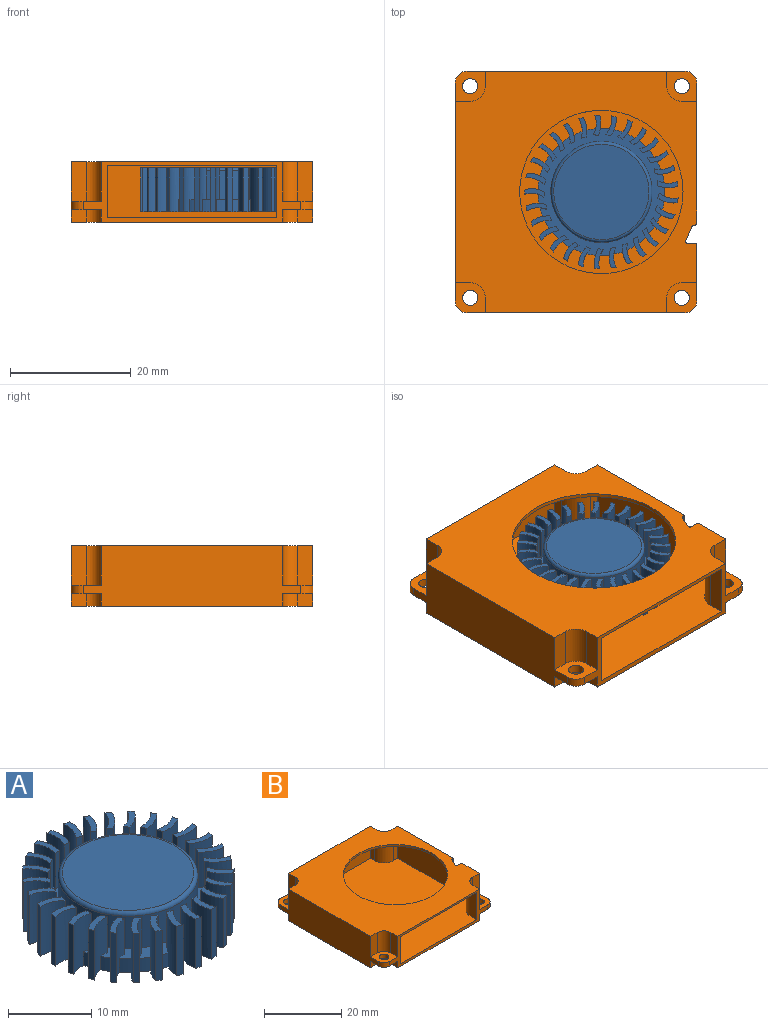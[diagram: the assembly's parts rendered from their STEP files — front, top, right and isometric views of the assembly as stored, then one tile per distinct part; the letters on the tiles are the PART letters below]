
ASSEMBLY  parts=2 mates=1
PART A: 179 faces, bbox 25.4x25.4x7.3 mm
  f0: plane 21x20.99mm, normal (0,0,1), area 101.2mm2, adj f1,f2,f3,f4,f5,f6,f7,f8
  f1: cylinder r=10.5mm len=2mm, axis (0,0,-1), area 3mm2, adj f0,f30,f172,f175
  f2: cylinder r=10.5mm len=2mm, axis (0,0,-1), area 3mm2, adj f0,f30,f167,f170
  f3: cylinder r=10.5mm len=2mm, axis (0,0,-1), area 3mm2, adj f0,f30,f162,f165
  f4: cylinder r=10.5mm len=2mm, axis (0,0,-1), area 3mm2, adj f0,f30,f157,f160
  f5: cylinder r=10.5mm len=2mm, axis (0,0,-1), area 3mm2, adj f0,f30,f152,f155
  f6: cylinder r=10.5mm len=2mm, axis (0,0,-1), area 3mm2, adj f0,f30,f147,f150
  f7: cylinder r=10.5mm len=2mm, axis (0,0,-1), area 3mm2, adj f0,f30,f142,f145
  f8: cylinder r=10.5mm len=2mm, axis (0,0,-1), area 3mm2, adj f0,f30,f137,f140
  f9: cylinder r=10.5mm len=2mm, axis (0,0,-1), area 3mm2, adj f0,f30,f132,f135
  f10: cylinder r=10.5mm len=2mm, axis (0,0,-1), area 3mm2, adj f0,f30,f127,f130
  f11: cylinder r=10.5mm len=2mm, axis (0,0,-1), area 3mm2, adj f0,f30,f122,f125
  f12: cylinder r=10.5mm len=2mm, axis (0,0,-1), area 3mm2, adj f0,f30,f117,f120
  f13: cylinder r=10.5mm len=2mm, axis (0,0,-1), area 3mm2, adj f0,f30,f112,f115
  f14: cylinder r=10.5mm len=2mm, axis (0,0,-1), area 3mm2, adj f0,f30,f107,f110
  f15: cylinder r=10.5mm len=2mm, axis (0,0,-1), area 3mm2, adj f0,f30,f102,f105
  f16: cylinder r=10.5mm len=2mm, axis (0,0,-1), area 3mm2, adj f0,f30,f97,f100
  f17: cylinder r=10.5mm len=2mm, axis (0,0,-1), area 3mm2, adj f0,f30,f92,f95
  f18: cylinder r=10.5mm len=2mm, axis (0,0,-1), area 3mm2, adj f0,f30,f87,f90
  f19: cylinder r=10.5mm len=2mm, axis (0,0,-1), area 3mm2, adj f0,f30,f82,f85
  f20: cylinder r=10.5mm len=2mm, axis (0,0,-1), area 3mm2, adj f0,f30,f77,f80
  f21: cylinder r=10.5mm len=2mm, axis (0,0,-1), area 3mm2, adj f0,f30,f72,f75
  f22: cylinder r=10.5mm len=2mm, axis (0,0,-1), area 3mm2, adj f0,f30,f67,f70
  f23: cylinder r=10.5mm len=2mm, axis (0,0,-1), area 3mm2, adj f0,f30,f62,f65
  f24: cylinder r=10.5mm len=2mm, axis (0,0,-1), area 3mm2, adj f0,f30,f57,f60
  f25: cylinder r=10.5mm len=2mm, axis (0,0,-1), area 3mm2, adj f0,f30,f52,f55
  f26: cylinder r=10.5mm len=2mm, axis (0,0,-1), area 3mm2, adj f0,f30,f47,f50
  f27: cylinder r=10.5mm len=2mm, axis (0,0,-1), area 3mm2, adj f0,f30,f42,f45
  f28: cylinder r=10.5mm len=2mm, axis (0,0,-1), area 3mm2, adj f0,f30,f34,f40
  f29: cylinder r=10.5mm len=2mm, axis (0,0,-1), area 3mm2, adj f0,f30,f33,f177
  f30: plane 25.4x25.4mm, normal (0,0,-1), area 394.2mm2, adj f1,f2,f3,f4,f5,f6,f7,f8
  f31: cylinder r=8.38mm len=16.75mm, axis (0,0,-1), area 250mm2, adj f0,f178
  f32: plane 15.75x15.75mm, normal (0,0,1), area 194.8mm2, adj f178
  f33: cylinder r=4.5mm len=7.25mm, axis (0,0,-1), area 21.8mm2, adj f0,f29,f30,f35,f36,f37
  f34: cylinder r=3.75mm len=7.25mm, axis (0,0,-1), area 22.2mm2, adj f0,f28,f30,f35,f36,f37
  f35: plane 3.36x1.87mm, normal (0,0,1), area 2.5mm2, adj f33,f34,f36,f37
  f36: plane 7.25x0.75mm, normal (-0.37,0.93,0), area 5.8mm2, adj f30,f33,f34,f35
  f37: plane 5.25x0.77mm, normal (0.37,-0.93,0), area 4.4mm2, adj f0,f33,f34,f35
  f38: plane 3.21x2.41mm, normal (0,0,1), area 2.5mm2, adj f39,f40,f41,f42
  f39: plane 7.25x0.67mm, normal (-0.56,0.83,0), area 5.8mm2, adj f30,f38,f40,f42
  f40: cylinder r=4.5mm len=7.25mm, axis (0,0,-1), area 21.8mm2, adj f0,f28,f30,f38,f39,f41
  f41: plane 5.25x0.69mm, normal (0.56,-0.83,0), area 4.4mm2, adj f0,f38,f40,f42
  f42: cylinder r=3.75mm len=7.25mm, axis (0,0,-1), area 22.2mm2, adj f0,f27,f30,f38,f39,f41
  f43: plane 2.91x2.85mm, normal (0,0,1), area 2.5mm2, adj f44,f45,f46,f47
  f44: plane 7.25x0.59mm, normal (-0.73,0.69,0), area 5.8mm2, adj f30,f43,f45,f47
  f45: cylinder r=4.5mm len=7.25mm, axis (0,0,-1), area 21.8mm2, adj f0,f27,f30,f43,f44,f46
  f46: plane 5.25x0.6mm, normal (0.73,-0.69,0), area 4.4mm2, adj f0,f43,f45,f47
  f47: cylinder r=3.75mm len=7.25mm, axis (0,0,-1), area 22.2mm2, adj f0,f26,f30,f43,f44,f46
  f48: plane 3.15x2.47mm, normal (0,0,1), area 2.5mm2, adj f49,f50,f51,f52
  f49: plane 7.25x0.69mm, normal (-0.86,0.51,0), area 5.8mm2, adj f30,f48,f50,f52
  f50: cylinder r=4.5mm len=7.25mm, axis (0,0,-1), area 21.8mm2, adj f0,f26,f30,f48,f49,f51
  f51: plane 5.25x0.71mm, normal (0.86,-0.51,0), area 4.4mm2, adj f0,f48,f50,f52
  f52: cylinder r=3.75mm len=7.25mm, axis (0,0,-1), area 22.2mm2, adj f0,f25,f30,f48,f49,f51
  f53: plane 3.31x1.91mm, normal (0,0,1), area 2.5mm2, adj f54,f55,f56,f57
  f54: plane 7.25x0.76mm, normal (-0.95,0.32,0), area 5.8mm2, adj f30,f53,f55,f57
  f55: cylinder r=4.5mm len=7.25mm, axis (0,0,-1), area 21.8mm2, adj f0,f25,f30,f53,f54,f56
  f56: plane 5.25x0.79mm, normal (0.95,-0.32,0), area 4.4mm2, adj f0,f53,f55,f57
  f57: cylinder r=3.75mm len=7.25mm, axis (0,0,-1), area 22.2mm2, adj f0,f24,f30,f53,f54,f56
  f58: plane 3.31x1.39mm, normal (0,0,1), area 2.5mm2, adj f59,f60,f61,f62
  f59: plane 7.25x0.8mm, normal (-0.99,0.11,0), area 5.8mm2, adj f30,f58,f60,f62
  f60: cylinder r=4.5mm len=7.25mm, axis (0,0,-1), area 21.8mm2, adj f0,f24,f30,f58,f59,f61
  f61: plane 5.25x0.82mm, normal (0.99,-0.11,0), area 4.4mm2, adj f0,f58,f60,f62
  f62: cylinder r=3.75mm len=7.25mm, axis (0,0,-1), area 22.2mm2, adj f0,f23,f30,f58,f59,f61
  f63: plane 3.33x1.25mm, normal (0,0,1), area 2.5mm2, adj f64,f65,f66,f67
  f64: plane 7.25x0.8mm, normal (-0.99,-0.11,0), area 5.8mm2, adj f30,f63,f65,f67
  f65: cylinder r=4.5mm len=7.25mm, axis (0,0,-1), area 21.8mm2, adj f0,f23,f30,f63,f64,f66
  f66: plane 5.25x0.82mm, normal (0.99,0.11,0), area 4.4mm2, adj f0,f63,f65,f67
  f67: cylinder r=3.75mm len=7.25mm, axis (0,0,-1), area 22.2mm2, adj f0,f22,f30,f63,f64,f66
  f68: plane 3.38x1.73mm, normal (0,0,1), area 2.5mm2, adj f69,f70,f71,f72
  f69: plane 7.25x0.76mm, normal (-0.95,-0.32,0), area 5.8mm2, adj f30,f68,f70,f72
  f70: cylinder r=4.5mm len=7.25mm, axis (0,0,-1), area 21.8mm2, adj f0,f22,f30,f68,f69,f71
  f71: plane 5.25x0.79mm, normal (0.95,0.32,0), area 4.4mm2, adj f0,f68,f70,f72
  f72: cylinder r=3.75mm len=7.25mm, axis (0,0,-1), area 22.2mm2, adj f0,f21,f30,f68,f69,f71
  f73: plane 3.26x2.29mm, normal (0,0,1), area 2.5mm2, adj f74,f75,f76,f77
  f74: plane 7.25x0.69mm, normal (-0.86,-0.52,0), area 5.8mm2, adj f30,f73,f75,f77
  f75: cylinder r=4.5mm len=7.25mm, axis (0,0,-1), area 21.8mm2, adj f0,f21,f30,f73,f74,f76
  f76: plane 5.25x0.71mm, normal (0.86,0.52,0), area 4.4mm2, adj f0,f73,f75,f77
  f77: cylinder r=3.75mm len=7.25mm, axis (0,0,-1), area 22.2mm2, adj f0,f20,f30,f73,f74,f76
  f78: plane 2.99x2.75mm, normal (0,0,1), area 2.5mm2, adj f79,f80,f81,f82
  f79: plane 7.25x0.58mm, normal (-0.73,-0.69,0), area 5.8mm2, adj f30,f78,f80,f82
  f80: cylinder r=4.5mm len=7.25mm, axis (0,0,-1), area 21.8mm2, adj f0,f20,f30,f78,f79,f81
  f81: plane 5.25x0.6mm, normal (0.73,0.69,0), area 4.4mm2, adj f0,f78,f80,f82
  f82: cylinder r=3.75mm len=7.25mm, axis (0,0,-1), area 22.2mm2, adj f0,f19,f30,f78,f79,f81
  f83: plane 3.09x2.59mm, normal (0,0,1), area 2.5mm2, adj f84,f85,f86,f87
  f84: plane 7.25x0.67mm, normal (-0.56,-0.83,0), area 5.8mm2, adj f30,f83,f85,f87
  f85: cylinder r=4.5mm len=7.25mm, axis (0,0,-1), area 21.8mm2, adj f0,f19,f30,f83,f84,f86
  f86: plane 5.25x0.69mm, normal (0.56,0.83,0), area 4.4mm2, adj f0,f83,f85,f87
  f87: cylinder r=3.75mm len=7.25mm, axis (0,0,-1), area 22.2mm2, adj f0,f18,f30,f83,f84,f86
  f88: plane 3.28x2.06mm, normal (0,0,1), area 2.5mm2, adj f89,f90,f91,f92
  f89: plane 7.25x0.75mm, normal (-0.37,-0.93,0), area 5.8mm2, adj f30,f88,f90,f92
  f90: cylinder r=4.5mm len=7.25mm, axis (0,0,-1), area 21.8mm2, adj f0,f18,f30,f88,f89,f91
  f91: plane 5.25x0.77mm, normal (0.37,0.93,0), area 4.4mm2, adj f0,f88,f90,f92
  f92: cylinder r=3.75mm len=7.25mm, axis (0,0,-1), area 22.2mm2, adj f0,f17,f30,f88,f89,f91
  f93: plane 3.32x1.51mm, normal (0,0,1), area 2.5mm2, adj f94,f95,f96,f97
  f94: plane 7.25x0.8mm, normal (-0.16,-0.99,0), area 5.8mm2, adj f30,f93,f95,f97
  f95: cylinder r=4.5mm len=7.25mm, axis (0,0,-1), area 21.8mm2, adj f0,f17,f30,f93,f94,f96
  f96: plane 5.25x0.82mm, normal (0.16,0.99,0), area 4.4mm2, adj f0,f93,f95,f97
  f97: cylinder r=3.75mm len=7.25mm, axis (0,0,-1), area 22.2mm2, adj f0,f16,f30,f93,f94,f96
  f98: plane 3.3x1.15mm, normal (0,0,1), area 2.5mm2, adj f99,f100,f101,f102
  f99: plane 7.25x0.8mm, normal (0.06,-1,0), area 5.8mm2, adj f30,f98,f100,f102
  f100: cylinder r=4.5mm len=7.25mm, axis (0,0,-1), area 21.8mm2, adj f0,f16,f30,f98,f99,f101
  f101: plane 5.25x0.83mm, normal (-0.06,1,0), area 4.4mm2, adj f0,f98,f100,f102
  f102: cylinder r=3.75mm len=7.25mm, axis (0,0,-1), area 22.2mm2, adj f0,f15,f30,f98,f99,f101
  f103: plane 3.38x1.59mm, normal (0,0,1), area 2.5mm2, adj f104,f105,f106,f107
  f104: plane 7.25x0.78mm, normal (0.27,-0.96,0), area 5.8mm2, adj f30,f103,f105,f107
  f105: cylinder r=4.5mm len=7.25mm, axis (0,0,-1), area 21.8mm2, adj f0,f15,f30,f103,f104,f106
  f106: plane 5.25x0.8mm, normal (-0.27,0.96,0), area 4.4mm2, adj f0,f103,f105,f107
  f107: cylinder r=3.75mm len=7.25mm, axis (0,0,-1), area 22.2mm2, adj f0,f14,f30,f103,f104,f106
  f108: plane 3.3x2.15mm, normal (0,0,1), area 2.5mm2, adj f109,f110,f111,f112
  f109: plane 7.25x0.71mm, normal (0.47,-0.88,0), area 5.8mm2, adj f30,f108,f110,f112
  f110: cylinder r=4.5mm len=7.25mm, axis (0,0,-1), area 21.8mm2, adj f0,f14,f30,f108,f109,f111
  f111: plane 5.25x0.73mm, normal (-0.47,0.88,0), area 4.4mm2, adj f0,f108,f110,f112
  f112: cylinder r=3.75mm len=7.25mm, axis (0,0,-1), area 22.2mm2, adj f0,f13,f30,f108,f109,f111
  f113: plane 3.08x2.65mm, normal (0,0,1), area 2.5mm2, adj f114,f115,f116,f117
  f114: plane 7.25x0.61mm, normal (0.65,-0.76,0), area 5.8mm2, adj f30,f113,f115,f117
  f115: cylinder r=4.5mm len=7.25mm, axis (0,0,-1), area 21.8mm2, adj f0,f13,f30,f113,f114,f116
  f116: plane 5.25x0.63mm, normal (-0.65,0.76,0), area 4.4mm2, adj f0,f113,f115,f117
  f117: cylinder r=3.75mm len=7.25mm, axis (0,0,-1), area 22.2mm2, adj f0,f12,f30,f113,f114,f116
  f118: plane 3.02x2.7mm, normal (0,0,1), area 2.5mm2, adj f119,f120,f121,f122
  f119: plane 7.25x0.64mm, normal (0.8,-0.6,0), area 5.8mm2, adj f30,f118,f120,f122
  f120: cylinder r=4.5mm len=7.25mm, axis (0,0,-1), area 21.8mm2, adj f0,f12,f30,f118,f119,f121
  f121: plane 5.25x0.66mm, normal (-0.8,0.6,0), area 4.4mm2, adj f0,f118,f120,f122
  f122: cylinder r=3.75mm len=7.25mm, axis (0,0,-1), area 22.2mm2, adj f0,f11,f30,f118,f119,f121
  f123: plane 3.25x2.2mm, normal (0,0,1), area 2.5mm2, adj f124,f125,f126,f127
  f124: plane 7.25x0.73mm, normal (0.91,-0.42,0), area 5.8mm2, adj f30,f123,f125,f127
  f125: cylinder r=4.5mm len=7.25mm, axis (0,0,-1), area 21.8mm2, adj f0,f11,f30,f123,f124,f126
  f126: plane 5.25x0.75mm, normal (-0.91,0.42,0), area 4.4mm2, adj f0,f123,f125,f127
  f127: cylinder r=3.75mm len=7.25mm, axis (0,0,-1), area 22.2mm2, adj f0,f10,f30,f123,f124,f126
  f128: plane 3.33x1.63mm, normal (0,0,1), area 2.5mm2, adj f129,f130,f131,f132
  f129: plane 7.25x0.79mm, normal (0.98,-0.21,0), area 5.8mm2, adj f30,f128,f130,f132
  f130: cylinder r=4.5mm len=7.25mm, axis (0,0,-1), area 21.8mm2, adj f0,f10,f30,f128,f129,f131
  f131: plane 5.25x0.81mm, normal (-0.98,0.21,0), area 4.4mm2, adj f0,f128,f130,f132
  f132: cylinder r=3.75mm len=7.25mm, axis (0,0,-1), area 22.2mm2, adj f0,f9,f30,f128,f129,f131
  f133: plane 3.25x1.18mm, normal (0,0,1), area 2.5mm2, adj f134,f135,f136,f137
  f134: plane 7.25x0.81mm, normal (1,0,0), area 5.8mm2, adj f30,f133,f135,f137
  f135: cylinder r=4.5mm len=7.25mm, axis (0,0,-1), area 21.8mm2, adj f0,f9,f30,f133,f134,f136
  f136: plane 5.25x0.83mm, normal (-1,0,0), area 4.4mm2, adj f0,f133,f135,f137
  f137: cylinder r=3.75mm len=7.25mm, axis (0,0,-1), area 22.2mm2, adj f0,f8,f30,f133,f134,f136
  f138: plane 3.37x1.47mm, normal (0,0,1), area 2.5mm2, adj f139,f140,f141,f142
  f139: plane 7.25x0.79mm, normal (0.98,0.22,0), area 5.8mm2, adj f30,f138,f140,f142
  f140: cylinder r=4.5mm len=7.25mm, axis (0,0,-1), area 21.8mm2, adj f0,f8,f30,f138,f139,f141
  f141: plane 5.25x0.81mm, normal (-0.98,-0.22,0), area 4.4mm2, adj f0,f138,f140,f142
  f142: cylinder r=3.75mm len=7.25mm, axis (0,0,-1), area 22.2mm2, adj f0,f7,f30,f138,f139,f141
  f143: plane 3.34x2.01mm, normal (0,0,1), area 2.5mm2, adj f144,f145,f146,f147
  f144: plane 7.25x0.73mm, normal (0.91,0.42,0), area 5.8mm2, adj f30,f143,f145,f147
  f145: cylinder r=4.5mm len=7.25mm, axis (0,0,-1), area 21.8mm2, adj f0,f7,f30,f143,f144,f146
  f146: plane 5.25x0.75mm, normal (-0.91,-0.42,0), area 4.4mm2, adj f0,f143,f145,f147
  f147: cylinder r=3.75mm len=7.25mm, axis (0,0,-1), area 22.2mm2, adj f0,f6,f30,f143,f144,f146
  f148: plane 3.15x2.53mm, normal (0,0,1), area 2.5mm2, adj f149,f150,f151,f152
  f149: plane 7.25x0.64mm, normal (0.8,0.61,0), area 5.8mm2, adj f30,f148,f150,f152
  f150: cylinder r=4.5mm len=7.25mm, axis (0,0,-1), area 21.8mm2, adj f0,f6,f30,f148,f149,f151
  f151: plane 5.25x0.66mm, normal (-0.8,-0.61,0), area 4.4mm2, adj f0,f148,f150,f152
  f152: cylinder r=3.75mm len=7.25mm, axis (0,0,-1), area 22.2mm2, adj f0,f5,f30,f148,f149,f151
  f153: plane 2.94x2.81mm, normal (0,0,1), area 2.5mm2, adj f154,f155,f156,f157
  f154: plane 7.25x0.61mm, normal (0.65,0.76,0), area 5.8mm2, adj f30,f153,f155,f157
  f155: cylinder r=4.5mm len=7.25mm, axis (0,0,-1), area 21.8mm2, adj f0,f5,f30,f153,f154,f156
  f156: plane 5.25x0.63mm, normal (-0.65,-0.76,0), area 4.4mm2, adj f0,f153,f155,f157
  f157: cylinder r=3.75mm len=7.25mm, axis (0,0,-1), area 22.2mm2, adj f0,f4,f30,f153,f154,f156
  f158: plane 3.2x2.34mm, normal (0,0,1), area 2.5mm2, adj f159,f160,f161,f162
  f159: plane 7.25x0.71mm, normal (0.47,0.88,0), area 5.8mm2, adj f30,f158,f160,f162
  f160: cylinder r=4.5mm len=7.25mm, axis (0,0,-1), area 21.8mm2, adj f0,f4,f30,f158,f159,f161
  f161: plane 5.25x0.73mm, normal (-0.47,-0.88,0), area 4.4mm2, adj f0,f158,f160,f162
  f162: cylinder r=3.75mm len=7.25mm, axis (0,0,-1), area 22.2mm2, adj f0,f3,f30,f158,f159,f161
  f163: plane 3.32x1.77mm, normal (0,0,1), area 2.5mm2, adj f164,f165,f166,f167
  f164: plane 7.25x0.78mm, normal (0.27,0.96,0), area 5.8mm2, adj f30,f163,f165,f167
  f165: cylinder r=4.5mm len=7.25mm, axis (0,0,-1), area 21.8mm2, adj f0,f3,f30,f163,f164,f166
  f166: plane 5.25x0.8mm, normal (-0.27,-0.96,0), area 4.4mm2, adj f0,f163,f165,f167
  f167: cylinder r=3.75mm len=7.25mm, axis (0,0,-1), area 22.2mm2, adj f0,f2,f30,f163,f164,f166
  f168: plane 3.28x1.28mm, normal (0,0,1), area 2.5mm2, adj f169,f170,f171,f172
  f169: plane 7.25x0.8mm, normal (0.05,1,0), area 5.8mm2, adj f30,f168,f170,f172
  f170: cylinder r=4.5mm len=7.25mm, axis (0,0,-1), area 21.8mm2, adj f0,f2,f30,f168,f169,f171
  f171: plane 5.25x0.83mm, normal (-0.05,-1,0), area 4.4mm2, adj f0,f168,f170,f172
  f172: cylinder r=3.75mm len=7.25mm, axis (0,0,-1), area 22.2mm2, adj f0,f1,f30,f168,f169,f171
  f173: plane 3.36x1.35mm, normal (0,0,1), area 2.5mm2, adj f174,f175,f176,f177
  f174: plane 7.25x0.8mm, normal (-0.16,0.99,0), area 5.8mm2, adj f30,f173,f175,f177
  f175: cylinder r=4.5mm len=7.25mm, axis (0,0,-1), area 21.8mm2, adj f0,f1,f30,f173,f174,f176
  f176: plane 5.25x0.82mm, normal (0.16,-0.99,0), area 4.4mm2, adj f0,f173,f175,f177
  f177: cylinder r=3.75mm len=7.25mm, axis (0,0,-1), area 22.2mm2, adj f0,f29,f30,f173,f174,f176
  f178: torus R=7.88mm, axis (0,0,1), area 40.4mm2, adj f31,f32
PART B: 77 faces, bbox 40x40x10 mm
  f0: cylinder r=1.25mm len=2.5mm, axis (0,0,-1), area 11mm2, adj f51,f72
  f1: cylinder r=1.25mm len=2.5mm, axis (0,0,-1), area 11mm2, adj f56,f60
  f2: plane 6.5x2.5mm, normal (0,1,0), area 16.3mm2, adj f3,f36,f42,f56
  f3: cylinder r=2.5mm len=6.5mm, axis (0,0,-1), area 25.5mm2, adj f2,f4,f42,f56
  f4: plane 6.5x2.5mm, normal (1,0,0), area 16.2mm2, adj f3,f37,f42,f56
  f5: plane 6.5x2.5mm, normal (0,-1,0), area 16.3mm2, adj f6,f41,f42,f51
  f6: cylinder r=2.5mm len=6.5mm, axis (0,0,-1), area 25.5mm2, adj f5,f7,f42,f51
  f7: plane 6.5x2.5mm, normal (-1,0,0), area 16.2mm2, adj f6,f28,f42,f51
  f8: cylinder r=1.3mm len=8.6mm, axis (0,0,1), area 9.2mm2, adj f9,f27,f48,f49
  f9: plane 8.6x2.4mm, normal (-0.92,0.38,0), area 22.4mm2, adj f8,f10,f48,f49
  f10: cylinder r=1.3mm len=8.6mm, axis (0,0,1), area 22mm2, adj f9,f11,f48,f49
  f11: plane 8.6x0.55mm, normal (0,-1,0), area 4.7mm2, adj f10,f12,f48,f49
  f12: plane 8.6x4.5mm, normal (-1,0,0), area 38.7mm2, adj f11,f13,f48,f49
  f13: plane 8.6x1.5mm, normal (0,1,0), area 12.9mm2, adj f12,f14,f48,f49
  f14: cylinder r=3.5mm len=8.6mm, axis (0,0,1), area 47.3mm2, adj f13,f15,f48,f49
  f15: plane 8.6x2.5mm, normal (-1,0,0), area 21.5mm2, adj f14,f28,f48,f49
  f16: plane 8.6x2.5mm, normal (1,0,0), area 21.5mm2, adj f17,f28,f48,f49
  f17: cylinder r=3.5mm len=8.6mm, axis (0,0,1), area 47.3mm2, adj f16,f18,f48,f49
  f18: plane 8.6x1.5mm, normal (0,1,0), area 12.9mm2, adj f17,f19,f48,f49
  f19: plane 28x8.6mm, normal (1,0,0), area 240.8mm2, adj f18,f20,f48,f49
  f20: plane 8.6x1.5mm, normal (0,-1,0), area 12.9mm2, adj f19,f21,f48,f49
  f21: cylinder r=3.5mm len=8.6mm, axis (0,0,1), area 47.3mm2, adj f20,f22,f48,f49
  f22: plane 8.6x1.5mm, normal (1,0,0), area 12.9mm2, adj f21,f23,f48,f49
  f23: plane 28x8.6mm, normal (0,-1,0), area 240.8mm2, adj f22,f24,f48,f49
  f24: plane 8.6x1.5mm, normal (-1,0,0), area 12.9mm2, adj f23,f25,f48,f49
  f25: cylinder r=3.5mm len=8.6mm, axis (0,0,1), area 47.3mm2, adj f24,f26,f48,f49
  f26: plane 8.6x1.5mm, normal (0,-1,0), area 12.9mm2, adj f25,f27,f48,f49
  f27: plane 18.58x8.6mm, normal (-1,0,0), area 159.8mm2, adj f8,f26,f48,f49
  f28: plane 36x10mm, normal (0,-1,0), area 67.6mm2, adj f7,f15,f16,f29,f42,f43,f48,f49
  f29: plane 6.5x2.5mm, normal (1,0,0), area 16.2mm2, adj f28,f30,f42,f54
  f30: cylinder r=2.5mm len=6.5mm, axis (0,0,-1), area 25.5mm2, adj f29,f31,f42,f54
  f31: plane 6.5x2.5mm, normal (0,-1,0), area 16.3mm2, adj f30,f32,f42,f54
  f32: plane 10x9.15mm, normal (1,0,0), area 65.7mm2, adj f31,f42,f43,f45,f54,f62,f64,f75
  f33: plane 10x1.2mm, normal (0,1,0), area 12mm2, adj f42,f43,f45,f47
  f34: plane 10x2.4mm, normal (0.92,-0.38,0), area 26mm2, adj f42,f43,f46,f47
  f35: plane 10x0.2mm, normal (0,-1,0), area 2mm2, adj f42,f43,f44,f46
  f36: plane 23.15x10mm, normal (1,0,0), area 205.7mm2, adj f2,f42,f43,f44,f56,f58,f60,f74
  f37: plane 36x10mm, normal (0,1,0), area 308.4mm2, adj f4,f38,f42,f43,f52,f56,f59,f60
  f38: plane 6.5x2.5mm, normal (-1,0,0), area 16.2mm2, adj f37,f39,f42,f52
  f39: cylinder r=2.5mm len=6.5mm, axis (0,0,-1), area 25.5mm2, adj f38,f40,f42,f52
  f40: plane 6.5x2.5mm, normal (0,1,0), area 16.3mm2, adj f39,f41,f42,f52
  f41: plane 36x10mm, normal (-1,0,0), area 308.4mm2, adj f5,f40,f42,f43,f51,f52,f65,f68
  f42: plane 40x40mm, normal (0,0,1), area 928.7mm2, adj f2,f3,f4,f5,f6,f7,f28,f29
  f43: plane 40x40mm, normal (0,0,-1), area 1501.2mm2, adj f28,f32,f33,f34,f35,f36,f37,f41
  f44: cylinder r=0.35mm len=10mm, axis (0,0,-1), area 5.5mm2, adj f35,f36,f42,f43
  f45: cylinder r=0.35mm len=10mm, axis (0,0,-1), area 5.5mm2, adj f32,f33,f42,f43
  f46: cylinder r=0.3mm len=10mm, axis (0,0,1), area 3.5mm2, adj f34,f35,f42,f43
  f47: cylinder r=0.3mm len=10mm, axis (0,0,1), area 5.9mm2, adj f33,f34,f42,f43
  f48: plane 39x38mm, normal (0,0,1), area 1376.2mm2, adj f8,f9,f10,f11,f12,f13,f14,f15
  f49: plane 39x38mm, normal (0,0,-1), area 803.7mm2, adj f8,f9,f10,f11,f12,f13,f14,f15
  f50: cylinder r=13.5mm len=27mm, axis (0,0,1), area 50.9mm2, adj f42,f49
  f51: plane 5x5mm, normal (0,0,1), area 17.9mm2, adj f0,f5,f6,f7,f28,f41,f76
  f52: plane 5x5mm, normal (0,0,1), area 17.9mm2, adj f37,f38,f39,f40,f41,f53,f73
  f53: cylinder r=1.25mm len=2.5mm, axis (0,0,-1), area 11mm2, adj f52,f68
  f54: plane 5x5mm, normal (0,0,1), area 17.9mm2, adj f28,f29,f30,f31,f32,f55,f75
  f55: cylinder r=1.25mm len=2.5mm, axis (0,0,-1), area 11mm2, adj f54,f64
  f56: plane 5x5mm, normal (0,0,1), area 17.9mm2, adj f1,f2,f3,f4,f36,f37,f74
  f57: cylinder r=2.5mm len=2.5mm, axis (0,0,-1), area 8.2mm2, adj f43,f58,f59,f60
  f58: plane 2.5x2.1mm, normal (0,1,0), area 5.3mm2, adj f36,f43,f57,f60
  f59: plane 2.5x2.1mm, normal (1,0,0), area 5.2mm2, adj f37,f43,f57,f60
  f60: plane 5x5mm, normal (0,0,-1), area 17.9mm2, adj f1,f36,f37,f57,f58,f59,f74
  f61: plane 2.5x2.1mm, normal (1,0,0), area 5.2mm2, adj f28,f43,f63,f64
  f62: plane 2.5x2.1mm, normal (0,-1,0), area 5.3mm2, adj f32,f43,f63,f64
  f63: cylinder r=2.5mm len=2.5mm, axis (0,0,-1), area 8.2mm2, adj f43,f61,f62,f64
  f64: plane 5x5mm, normal (0,0,-1), area 17.9mm2, adj f28,f32,f55,f61,f62,f63,f75
  f65: plane 2.5x2.1mm, normal (0,1,0), area 5.2mm2, adj f41,f43,f66,f68
  f66: cylinder r=2.5mm len=2.5mm, axis (0,0,-1), area 8.2mm2, adj f43,f65,f67,f68
  f67: plane 2.5x2.1mm, normal (-1,0,0), area 5.2mm2, adj f37,f43,f66,f68
  f68: plane 5x5mm, normal (0,0,-1), area 17.9mm2, adj f37,f41,f53,f65,f66,f67,f73
  f69: plane 2.5x2.1mm, normal (-1,0,0), area 5.2mm2, adj f28,f43,f70,f72
  f70: cylinder r=2.5mm len=2.5mm, axis (0,0,-1), area 8.2mm2, adj f43,f69,f71,f72
  f71: plane 2.5x2.1mm, normal (0,-1,0), area 5.2mm2, adj f41,f43,f70,f72
  f72: plane 5x5mm, normal (0,0,-1), area 17.9mm2, adj f0,f28,f41,f69,f70,f71,f76
  f73: cylinder r=2mm len=2mm, axis (0,0,-1), area 4.4mm2, adj f37,f41,f52,f68
  f74: cylinder r=2mm len=2mm, axis (0,0,1), area 4.4mm2, adj f36,f37,f56,f60
  f75: cylinder r=2mm len=2mm, axis (0,0,-1), area 4.4mm2, adj f28,f32,f54,f64
  f76: cylinder r=2mm len=2mm, axis (0,0,1), area 4.4mm2, adj f28,f41,f51,f72
PLACE A t=(0,0,-1)mm
PLACE B at identity
MATE fastened A.f1 <-> B.f50  axis (0,0,1) through (25.79,27.41,24.29)mm
